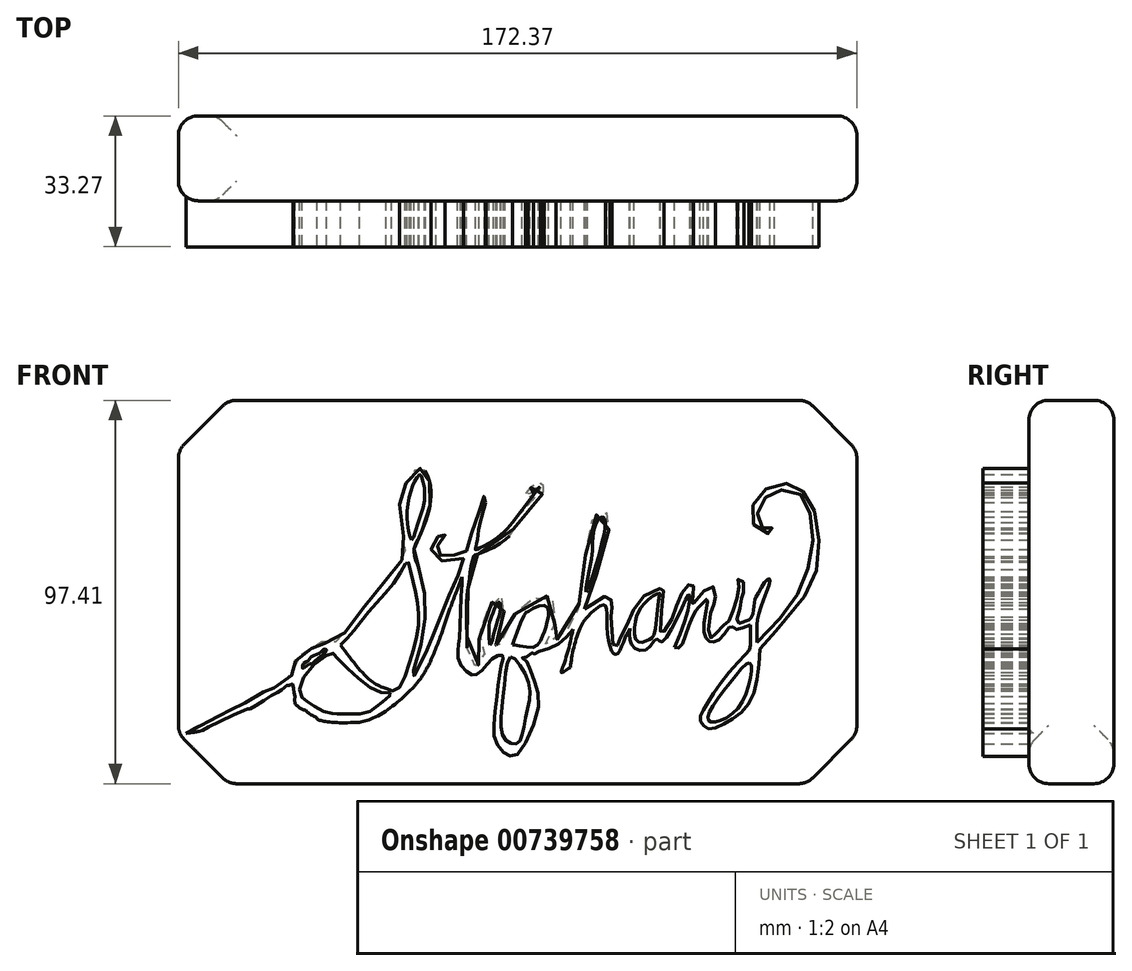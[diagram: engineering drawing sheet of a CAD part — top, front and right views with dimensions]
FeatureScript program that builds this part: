
annotation { "Feature Type Name" : "Feature", "Feature Type Description" : "" }
export const myFeature = defineFeature(function(context is Context, id is Id, definition is map)
    precondition{}
    {
        {
            var Q0;
            Q0=qCreatedBy(makeId("Front.planeOp"),FACE);
            var sketch = newSketch(context, id + "F0", { "sketchPlane" : qUnion([Q0])});
            skFitSpline(sketch, "E0", {"points": [v(-101.57, -22.4) * mm, v(-98.14, -21.93) * mm, v(-96.48, -21.22) * mm, v(-86.08, -16.25) * mm, v(-85.85, -16.25) * mm, v(-85.52, -16.34) * mm, v(-80.65, -13.35) * mm, v(-77.6, -11.6) * mm, v(-76.48, -10.68) * mm, v(-75.94, -10.23) * mm, v(-75.67, -10.38) * mm, v(-74.63, -9.9) * mm, v(-74.23, -11.35) * mm, v(-73.93, -12.77) * mm, v(-73.93, -13.86) * mm, v(-73.9, -14.88) * mm], "startDerivative": vector(43.72, 5.03) * mm, "endDerivative": vector(1, -20.05) * mm});
            skFitSpline(sketch, "E1", {"points": [v(-73.9, -14.88) * mm, v(-72.34, -16.17) * mm, v(-71.05, -16.67) * mm, v(-70.8, -16.98) * mm, v(-68.22, -18.5) * mm], "startDerivative": vector(4.71, -5.08) * mm, "endDerivative": vector(10.26, -4.06) * mm});
            skFitSpline(sketch, "E2", {"points": [v(-68.22, -18.5) * mm, v(-68.22, -18.92) * mm, v(-67.8, -19.07) * mm, v(-65.06, -19.6) * mm, v(-57.5, -19.64) * mm], "startDerivative": vector(-0.75, -4.39) * mm, "endDerivative": vector(17.3, 0.6) * mm});
            skFitSpline(sketch, "E3", {"points": [v(-57.5, -19.64) * mm, v(-54.54, -18.8) * mm, v(-49.42, -15.75) * mm, v(-44.72, -11.7) * mm], "startDerivative": vector(10.61, 2.2) * mm, "endDerivative": vector(12.02, 11.15) * mm});
            skFitSpline(sketch, "E4", {"points": [v(-44.72, -11.7) * mm, v(-42, -8.56) * mm, v(-39.49, -4.26) * mm], "startDerivative": vector(5.93, 6.19) * mm, "endDerivative": vector(4.56, 8.67) * mm});
            skFitSpline(sketch, "E5", {"points": [v(-39.49, -4.26) * mm, v(-36.9, 2.26) * mm, v(-35.5, 6.39) * mm], "startDerivative": vector(5.05, 12.3) * mm, "endDerivative": vector(2.83, 8.86) * mm});
            skFitSpline(sketch, "E6", {"points": [v(-35.5, 6.39) * mm, v(-34.1, 10.34) * mm, v(-31.83, 16.34) * mm], "startDerivative": vector(2.92, 8.4) * mm, "endDerivative": vector(4.39, 11.4) * mm});
            skLineSegment(sketch, "E7", {"start": v(-31.83, 16.34) * mm, "end": v(-31.44, 17.3) * mm});
            skLineSegment(sketch, "E8", {"start": v(-31.44, 17.3) * mm, "end": v(-31.42, 16.4) * mm});
            skFitSpline(sketch, "E9", {"points": [v(-31.42, 16.4) * mm, v(-31.51, 14.97) * mm, v(-31.7, 13.03) * mm, v(-32.14, 1.78) * mm, v(-32.38, -0.65) * mm, v(-32.27, -4.16) * mm, v(-29.57, -7.22) * mm, v(-28.03, -7.64) * mm, v(-25.78, -5.82) * mm, v(-23.25, -3.04) * mm, v(-21.2, -2.65) * mm, v(-20.96, -3.04) * mm, v(-21.66, -6.13) * mm, v(-22.59, -13.02) * mm], "startDerivative": vector(-1.55, -28.5) * mm, "endDerivative": vector(-6.13, -63.06) * mm});
            skFitSpline(sketch, "E10", {"points": [v(-22.59, -13.02) * mm, v(-23.35, -20.46) * mm, v(-22.97, -24.48) * mm, v(-20.92, -27.28) * mm, v(-19.12, -28.24) * mm, v(-17, -27.4) * mm, v(-12.19, -16.4) * mm, v(-12.73, -9.97) * mm, v(-14.48, -5.42) * mm, v(-15.4, -3.62) * mm, v(-16.22, -3.15) * mm, v(-14.88, -2.9) * mm, v(-13.6, -1.98) * mm, v(-13.39, -2.35) * mm, v(-12.94, -2.18) * mm, v(-12.5, -1.86) * mm, v(-9.48, -0.96) * mm, v(-5.8, 1.13) * mm, v(-3.23, 4) * mm], "startDerivative": vector(-10.48, -88.81) * mm, "endDerivative": vector(36.84, 47) * mm});
            skFitSpline(sketch, "E11", {"points": [v(-3.23, 4) * mm, v(-4.6, -1.77) * mm, v(-6.03, -6.14) * mm, v(-6.28, -6.94) * mm, v(-5.91, -6.9) * mm, v(-3.95, -5.64) * mm], "startDerivative": vector(-3.92, -18.07) * mm, "endDerivative": vector(11.23, 7.94) * mm});
            skFitSpline(sketch, "E12", {"points": [v(-3.95, -5.64) * mm, v(-2.9, 0) * mm, v(-0.68, 5.71) * mm, v(0.47, 7.13) * mm], "startDerivative": vector(1.9, 13.42) * mm, "endDerivative": vector(6.54, 6.93) * mm});
            skFitSpline(sketch, "E13", {"points": [v(0.47, 7.13) * mm, v(4.74, 10.18) * mm, v(5.34, 5.48) * mm, v(6.9, -2.06) * mm, v(8.06, -2.18) * mm, v(9.8, 1.34) * mm, v(11.22, 4.2) * mm], "startDerivative": vector(19.16, 25.63) * mm, "endDerivative": vector(9.64, 17.4) * mm});
            skFitSpline(sketch, "E14", {"points": [v(11.22, 4.2) * mm, v(11.22, 1.06) * mm, v(12.72, -0.95) * mm, v(15.65, -1) * mm, v(17.82, 1.47) * mm, v(18.53, 1.3) * mm, v(19.2, 0.76) * mm, v(23.55, 7.58) * mm, v(26.22, 12.82) * mm, v(26.47, 12.03) * mm, v(22.54, -0.65) * mm], "startDerivative": vector(-3.77, -34.47) * mm, "endDerivative": vector(-34.06, -74.18) * mm});
            skFitSpline(sketch, "E15", {"points": [v(22.54, -0.65) * mm, v(23.84, -0.65) * mm, v(26.12, 4.82) * mm, v(28.2, 9.13) * mm, v(29.37, 10.35) * mm, v(30.85, 11.63) * mm, v(30, 5.42) * mm, v(30.75, 1.47) * mm, v(31.99, 0.76) * mm, v(34.18, 1.6) * mm, v(36.94, 4.79) * mm, v(38.15, 4) * mm, v(41.79, 5.07) * mm], "startDerivative": vector(24.35, -8.2) * mm, "endDerivative": vector(49.58, 15.23) * mm});
            skFitSpline(sketch, "E16", {"points": [v(41.79, 5.07) * mm, v(41.79, -0.66) * mm, v(41.08, -1.83) * mm, v(34.77, -8.95) * mm, v(30.3, -15.72) * mm, v(29, -18.49) * mm, v(29.79, -20.41) * mm, v(31.57, -21.29) * mm, v(36.12, -19.47) * mm, v(41.79, -14.21) * mm, v(44.24, -0.94) * mm], "startDerivative": vector(2.93, -66.86) * mm, "endDerivative": vector(6.2, 92.79) * mm});
            skFitSpline(sketch, "E17", {"points": [v(44.24, -0.94) * mm, v(44.24, -0.77) * mm, v(54.9, 11.34) * mm, v(58.77, 20.35) * mm, v(58.77, 31.23) * mm, v(56.02, 38) * mm, v(52.89, 40.6) * mm, v(48.13, 40.88) * mm, v(43.7, 37.7) * mm, v(42.15, 33.61) * mm, v(43.27, 29.6) * mm, v(46.5, 28.35) * mm, v(47.98, 29.05) * mm, v(47.29, 29.68) * mm, v(46.12, 29.4) * mm, v(45.08, 29.53) * mm, v(43.92, 31.1) * mm, v(43.96, 35.06) * mm, v(46, 37.8) * mm, v(49.44, 39.36) * mm, v(53.97, 38.6) * mm, v(56.55, 35.03) * mm, v(57.7, 26.88) * mm, v(55.9, 17.78) * mm, v(51.66, 9.62) * mm, v(43.48, 0.72) * mm], "startDerivative": vector(-15.4, 31.3) * mm, "endDerivative": vector(-140.72, -139.71) * mm});
            skFitSpline(sketch, "E18", {"points": [v(43.48, 0.72) * mm, v(43.48, 5.07) * mm, v(44.68, 10.31) * mm, v(46.8, 16.4) * mm, v(46.48, 16.9) * mm, v(45.77, 16.3) * mm, v(43.48, 12.65) * mm, v(42.96, 11.36) * mm, v(42.7, 9.77) * mm, v(42.41, 7.76) * mm, v(41.47, 6.39) * mm], "startDerivative": vector(-0.95, 29.37) * mm, "endDerivative": vector(-7.68, -4.47) * mm});
            skFitSpline(sketch, "E19", {"points": [v(41.47, 6.39) * mm, v(38.66, 5.52) * mm, v(38.33, 6.39) * mm, v(39.33, 9.74) * mm, v(39.68, 12.45) * mm, v(40.12, 13.68) * mm, v(39.64, 16.7) * mm, v(38.63, 16.6) * mm, v(38.87, 14.5) * mm, v(37.76, 9.9) * mm, v(36.32, 6.05) * mm, v(35.28, 5.18) * mm, v(32.84, 2.73) * mm, v(31.8, 1.8) * mm, v(31.15, 3.47) * mm, v(32.37, 10.08) * mm, v(32.78, 10.72) * mm, v(32.73, 14.1) * mm, v(31.48, 14.86) * mm, v(27.26, 10.39) * mm, v(27.15, 10.17) * mm, v(27, 10.8) * mm, v(27.27, 12.47) * mm], "startDerivative": vector(-66, -30.26) * mm, "endDerivative": vector(11.12, 43.94) * mm});
            skFitSpline(sketch, "E20", {"points": [v(27.27, 12.47) * mm, v(27.27, 15.06) * mm, v(26.6, 15.49) * mm, v(25.62, 14.87) * mm, v(23.38, 10.97) * mm, v(21.58, 6.13) * mm, v(19.2, 2.88) * mm, v(18.94, 3.62) * mm, v(19.78, 14.11) * mm, v(19.81, 14.5) * mm, v(14.3, 12.11) * mm, v(10.67, 5.42) * mm, v(8.47, 1.06) * mm, v(7.93, -0.24) * mm, v(7.26, -0.4) * mm, v(6.63, 2.9) * mm, v(6.46, 8.07) * mm, v(6.63, 9.93) * mm, v(6.42, 11.4) * mm, v(5.4, 12.47) * mm, v(0.9, 9.8) * mm, v(-0.33, 9.13) * mm], "startDerivative": vector(8.54, 68.3) * mm, "endDerivative": vector(-28.47, -10.98) * mm});
            skFitSpline(sketch, "E21", {"points": [v(-0.33, 9.13) * mm, v(0.41, 10.84) * mm, v(1.92, 15.27) * mm, v(4.39, 23.8) * mm, v(5.87, 29.35) * mm, v(6.06, 32.45) * mm, v(4.74, 33.9) * mm, v(2.18, 32.65) * mm, v(0.8, 29.05) * mm, v(-0.33, 20.3) * mm, v(-1.42, 12.03) * mm, v(-2.37, 7.86) * mm, v(-5.51, 2.96) * mm, v(-10.23, 0) * mm, v(-8.7, 2.8) * mm, v(-7.55, 7.58) * mm, v(-8.2, 11.21) * mm, v(-10.09, 12.47) * mm, v(-14.21, 11.46) * mm, v(-17.79, 8.18) * mm, v(-22.02, 0) * mm, v(-22.76, -0.57) * mm, v(-22.46, 1.91) * mm, v(-21.52, 4.79) * mm, v(-20.57, 9.67) * mm, v(-20.82, 12.03) * mm, v(-22.11, 12.47) * mm, v(-24.8, 9.26) * mm, v(-26.59, 4.79) * mm, v(-26.89, 0) * mm, v(-25.7, -2.31) * mm, v(-26.74, -4.65) * mm, v(-28.13, -5.34) * mm, v(-29.42, -4.8) * mm, v(-30.22, 2.73) * mm, v(-30.32, 10.76) * mm, v(-29.49, 17.62) * mm, v(-28.4, 22.8) * mm, v(-27.5, 23.04) * mm, v(-20.1, 27.02) * mm, v(-17.91, 30.08) * mm, v(-12.5, 36.34) * mm, v(-10.73, 39.14) * mm, v(-10.8, 40.6) * mm, v(-11.79, 41) * mm, v(-13.83, 40.16) * mm, v(-15.23, 38.44) * mm, v(-15.2, 37.8) * mm, v(-14.67, 37.49) * mm, v(-13.5, 38.09) * mm, v(-13.37, 38.79) * mm, v(-14.18, 38.44) * mm, v(-14.63, 38.37) * mm, v(-14, 39.28) * mm, v(-11.61, 40.05) * mm, v(-11.9, 39.07) * mm, v(-18.6, 31.13) * mm], "startDerivative": vector(53.01, 116.38) * mm, "endDerivative": vector(-269.3, -302) * mm});
            skFitSpline(sketch, "E22", {"points": [v(-18.6, 31.13) * mm, v(-23.09, 26.8) * mm, v(-28.02, 24.24) * mm, v(-27.96, 24.5) * mm, v(-27.23, 29.05) * mm, v(-25.45, 36.24) * mm], "startDerivative": vector(-14.9, -17.86) * mm, "endDerivative": vector(7.64, 26.85) * mm});
            skFitSpline(sketch, "E23", {"points": [v(-25.45, 36.24) * mm, v(-25.45, 38) * mm, v(-25.62, 38.1) * mm, v(-26.25, 37.08) * mm, v(-27.43, 32.9) * mm, v(-29.49, 26.99) * mm, v(-30.44, 23.8) * mm, v(-32.27, 23.03) * mm, v(-34.24, 22.68) * mm, v(-36.92, 22.73) * mm, v(-38, 23.94) * mm, v(-37.42, 25.57) * mm, v(-36, 27.45) * mm, v(-35.79, 28.37) * mm, v(-36.76, 28.23) * mm, v(-38.04, 26.74) * mm, v(-39.3, 24.27) * mm, v(-37.92, 21.56) * mm, v(-31.23, 22.06) * mm, v(-31.36, 20.85) * mm, v(-33.51, 15.17) * mm, v(-35.79, 10.18) * mm, v(-38.5, 2.73) * mm, v(-39.64, 0.76) * mm, v(-41.82, -4.59) * mm, v(-44.42, -8.67) * mm, v(-43.18, -4.7) * mm, v(-41.17, 4) * mm, v(-40.82, 12.03) * mm, v(-42.36, 19.17) * mm], "startDerivative": vector(6.75, 88.7) * mm, "endDerivative": vector(-37.93, 136.76) * mm});
            skFitSpline(sketch, "E24", {"points": [v(-42.36, 19.17) * mm, v(-43.7, 23.89) * mm, v(-43, 26.06) * mm, v(-40.6, 31.69) * mm, v(-39.34, 37.66) * mm, v(-40.12, 42.94) * mm, v(-41.6, 44.83) * mm, v(-43.77, 44.06) * mm, v(-46.58, 38.72) * mm, v(-47.29, 34.43) * mm, v(-45.95, 24.03) * mm, v(-47.22, 20.93) * mm, v(-53.61, 13.06) * mm, v(-58.25, 7.01) * mm, v(-65.14, 0) * mm, v(-67.32, 0.83) * mm, v(-69.19, -0.48) * mm, v(-72.11, -2.26) * mm, v(-74.39, -5.88) * mm, v(-74.39, -7.37) * mm, v(-78.01, -9.86) * mm, v(-80.05, -11.45) * mm, v(-81.4, -11.55) * mm, v(-82.29, -12.34) * mm, v(-86.7, -14.82) * mm, v(-88.28, -15.67) * mm, v(-91.16, -16.9) * mm, v(-91.76, -17.46) * mm, v(-93.6, -18.25) * mm, v(-94.5, -18.75) * mm, v(-95.94, -19.4) * mm, v(-101.57, -22.4) * mm], "startDerivative": vector(-53.84, 142.45) * mm, "endDerivative": vector(-152.72, -84.73) * mm});
            skFitSpline(sketch, "E25", {"points": [v(-71.61, -5.78) * mm, v(-69.99, -4.8) * mm, v(-69.73, -4.8) * mm, v(-69.11, -4.34) * mm, v(-66.17, -1.78) * mm, v(-65.88, -1.22) * mm, v(-66.4, -1.03) * mm, v(-67.47, -1.96) * mm, v(-68.8, -2.54) * mm, v(-70.06, -3.36) * mm, v(-70.64, -4.09) * mm, v(-71.74, -4.8) * mm, v(-72, -5.86) * mm, v(-71.61, -5.78) * mm]});
            skFitSpline(sketch, "E26", {"points": [v(-71.75, -8.21) * mm, v(-64.6, -2) * mm, v(-63.83, -2.48) * mm, v(-58.63, -7.74) * mm, v(-51.77, -12.05) * mm, v(-49.4, -12.35) * mm, v(-50.89, -13.89) * mm, v(-53.55, -15.9) * mm, v(-56.2, -17.32) * mm, v(-62.89, -17.43) * mm, v(-64, -17.5) * mm, v(-67.08, -16.6) * mm, v(-70.63, -14.36) * mm, v(-72.23, -13.18) * mm, v(-71.75, -8.21) * mm]});
            skFitSpline(sketch, "E27", {"points": [v(-62.35, 0) * mm, v(-58.48, 4.26) * mm, v(-53.5, 10.32) * mm, v(-47.74, 17.28) * mm, v(-45.25, 21.16) * mm, v(-44.36, 18.17) * mm, v(-42.97, 11.81) * mm, v(-42.57, 4.75) * mm, v(-44.56, -3.8) * mm, v(-48.14, -11.45) * mm, v(-50.72, -11.05) * mm], "startDerivative": vector(41.11, 31.02) * mm, "endDerivative": vector(-24.87, 19.5) * mm});
            skFitSpline(sketch, "E28", {"points": [v(-50.72, -11.05) * mm, v(-54.5, -9.17) * mm, v(-62.35, 0) * mm], "startDerivative": vector(-9.73, 3.32) * mm, "endDerivative": vector(-13.23, 17.57) * mm});
            skFitSpline(sketch, "E29", {"points": [v(-44.26, 26.69) * mm, v(-42.92, 30.02) * mm, v(-41.03, 36.68) * mm, v(-41.23, 41.1) * mm, v(-42.12, 43.3) * mm, v(-43.21, 42) * mm, v(-44.36, 39.31) * mm, v(-45.35, 34.43) * mm, v(-45.05, 29.32) * mm, v(-44.26, 26.69) * mm]});
            skFitSpline(sketch, "E30", {"points": [v(-24.3, 0) * mm, v(-23.2, 3.52) * mm, v(-21.9, 7.91) * mm, v(-21.78, 10.75) * mm, v(-22.41, 10.63) * mm, v(-23.96, 7.28) * mm, v(-24.54, 5.07) * mm, v(-24.3, 0) * mm]});
            skFitSpline(sketch, "E31", {"points": [v(-18.57, 0) * mm, v(-15.6, 7.7) * mm, v(-14.85, 8.45) * mm, v(-10.87, 10.08) * mm, v(-9.5, 8.75) * mm, v(-10, 5.2) * mm, v(-11.08, 1.93) * mm, v(-13.3, -0.53) * mm, v(-18.27, 0) * mm, v(-18.57, 0) * mm]});
            skFitSpline(sketch, "E32", {"points": [v(-19.11, -3.04) * mm, v(-20.59, -9.13) * mm, v(-21.48, -18.12) * mm, v(-20.89, -23.5) * mm, v(-18.93, -25.03) * mm, v(-17.16, -24.85) * mm, v(-16.1, -22.37) * mm, v(-14.8, -16.34) * mm, v(-14.32, -10.6) * mm, v(-16.98, -4.76) * mm, v(-19.11, -3.04) * mm]});
            skFitSpline(sketch, "E33", {"points": [v(0, 13.54) * mm, v(1.33, 21.2) * mm, v(1.92, 27.96) * mm, v(3.21, 32.03) * mm, v(4.46, 32.43) * mm, v(5, 30.69) * mm, v(4.01, 25.67) * mm, v(1.92, 18.06) * mm, v(0, 13.54) * mm]});
            skFitSpline(sketch, "E34", {"points": [v(12.58, 5.98) * mm, v(13.82, 9.3) * mm, v(16.78, 12.25) * mm, v(18.73, 13.13) * mm, v(18.61, 12.25) * mm, v(17.31, 2.61) * mm, v(16.37, 1.6) * mm, v(14.53, 0.72) * mm, v(12.7, 1.37) * mm, v(12.58, 5.98) * mm]});
            skFitSpline(sketch, "E35", {"points": [v(41.64, -4.5) * mm, v(37.09, -9.05) * mm, v(31.3, -17.44) * mm, v(31.3, -19.33) * mm, v(33.48, -19.45) * mm, v(38.8, -15.84) * mm, v(41.93, -7.57) * mm, v(41.64, -4.5) * mm]});
            skSolve(sketch);
        }
        {
            var Q0;
            Q0=makeQuery(id+"F0.imprint","IMPRINT",FACE,{"disambiguationData":[TD([[makeQuery(id+"F0.imprint","IMPRINT",EDGE,{"derivedFrom":sQuery(id+"F0.wireOp",EDGE,"E0")}),1.0]])]});
            extrude(context, id + "F1", {"entities" : qUnion([Q0]), "depth" : 11.68 * mm, "offsetDistance" : 25.4 * mm});
        }
        {
            var Q0;
            Q0=qCreatedBy(makeId("Front.planeOp"),FACE);
            var sketch = newSketch(context, id + "F2", { "sketchPlane" : qUnion([Q0])});
            skLineSegment(sketch, "E36.bottom", {"start": v(-103.5, 62.18) * mm, "end": v(68.87, 62.18) * mm});
            skLineSegment(sketch, "E36.top", {"start": v(-103.5, -35.23) * mm, "end": v(68.87, -35.23) * mm});
            skLineSegment(sketch, "E36.left", {"start": v(-103.5, 62.18) * mm, "end": v(-103.5, -35.23) * mm});
            skLineSegment(sketch, "E36.right", {"start": v(68.87, 62.18) * mm, "end": v(68.87, -35.23) * mm});
            skSolve(sketch);
        }
        {
            var Q0;
            Q0 = qSketchRegion(id + "F2", true);
            extrude(context, id + "F3", {"entities" : qUnion([Q0]), "operationType" : NewBodyOperationType.ADD, "oppositeDirection" : true, "depth" : 21.59 * mm, "offsetDistance" : 25.4 * mm});
        }
        {
            var Q0;
            Q0=makeQuery(id+"F3.opExtrude","SWEPT_EDGE",EDGE,{"disambiguationData":[OSD([sQuery(id+"F2.wireOp",EDGE,"E36.bottom"),sQuery(id+"F2.wireOp",EDGE,"E36.left")])]});
            var Q1;
            Q1=makeQuery(id+"F3.opExtrude","SWEPT_EDGE",EDGE,{"disambiguationData":[OSD([sQuery(id+"F2.wireOp",EDGE,"E36.top"),sQuery(id+"F2.wireOp",EDGE,"E36.left")])]});
            var Q2;
            Q2=makeQuery(id+"F3.opExtrude","SWEPT_EDGE",EDGE,{"disambiguationData":[OSD([sQuery(id+"F2.wireOp",EDGE,"E36.top"),sQuery(id+"F2.wireOp",EDGE,"E36.right")])]});
            var Q3;
            Q3=makeQuery(id+"F3.opExtrude","SWEPT_EDGE",EDGE,{"disambiguationData":[OSD([sQuery(id+"F2.wireOp",EDGE,"E36.bottom"),sQuery(id+"F2.wireOp",EDGE,"E36.right")])]});
            chamfer(context, id + "F4", {"entities" : qUnion([Q0, Q1, Q2, Q3]), "width" : 12.7 * mm, "tangentPropagation" : true});
        }
        {
            var Q0;
            Q0=makeQuery(id+"F3.opExtrude","SWEPT_FACE",FACE,{"disambiguationData":[OSD([sQuery(id+"F2.wireOp",EDGE,"E36.left")])]});
            var Q1;
            Q1=makeQuery(id+"F4.opChamfer","BLEND_FACE",FACE,{"disambiguationData":[OSD([sQuery(id+"F2.wireOp",EDGE,"E36.bottom"),sQuery(id+"F2.wireOp",EDGE,"E36.left")])]});
            var Q2;
            Q2=makeQuery(id+"F3.opExtrude","SWEPT_FACE",FACE,{"disambiguationData":[OSD([sQuery(id+"F2.wireOp",EDGE,"E36.bottom")])]});
            var Q3;
            Q3=makeQuery(id+"F3.opExtrude","SWEPT_FACE",FACE,{"disambiguationData":[OSD([sQuery(id+"F2.wireOp",EDGE,"E36.right")])]});
            var Q4;
            Q4=makeQuery(id+"F4.opChamfer","BLEND_FACE",FACE,{"disambiguationData":[OSD([sQuery(id+"F2.wireOp",EDGE,"E36.bottom"),sQuery(id+"F2.wireOp",EDGE,"E36.right")])]});
            var Q5;
            Q5=makeQuery(id+"F4.opChamfer","BLEND_FACE",FACE,{"disambiguationData":[OSD([sQuery(id+"F2.wireOp",EDGE,"E36.top"),sQuery(id+"F2.wireOp",EDGE,"E36.right")])]});
            var Q6;
            Q6=makeQuery(id+"F3.opExtrude","SWEPT_FACE",FACE,{"disambiguationData":[OSD([sQuery(id+"F2.wireOp",EDGE,"E36.top")])]});
            fillet(context, id + "F5", {"entities" : qUnion([Q0, Q1, Q2, Q3, Q4, Q5, Q6]), "radius" : 5.08 * mm, "tangentPropagation" : true, "allowEdgeOverflow" : false});
        }
    });
